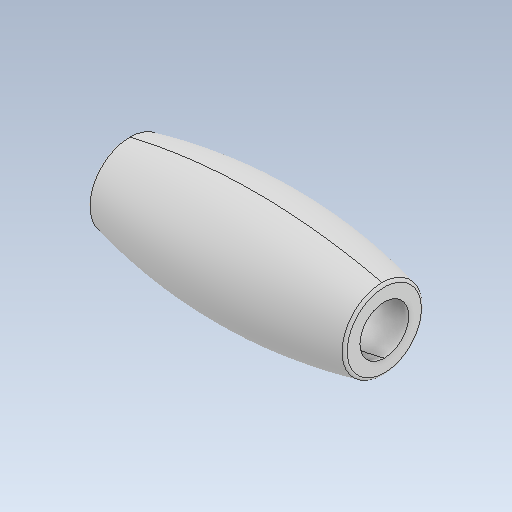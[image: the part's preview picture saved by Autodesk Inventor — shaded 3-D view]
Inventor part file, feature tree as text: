
AUTODESK INVENTOR PART (.ipt)
format: ipt  version: 2023 (Build 270158000, 158)  size: 177,664 bytes
history: native  units: in
note: dims shown in document units (in); Inventor stores cm internally (conversion verified against a paired STEP export)
features: other x1, fillet x1
ambient origin geometry x8: Origin, YZ Plane, XZ Plane, XY Plane, X Axis, Y Axis, Z Axis, Center Point
bodies: Solid1 (feature_tree)
feature tree (2):
  other  "4HD Mecanum roller skin.ipt1"
  fillet  "Fillet1"  [1 undecoded]
note: 1 required parameter value undecoded (feature->parameter linkage not recoverable at this tier; creation-order binding heuristic only, values carry confidence <= 0.55)
